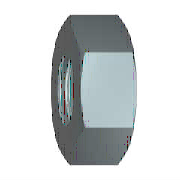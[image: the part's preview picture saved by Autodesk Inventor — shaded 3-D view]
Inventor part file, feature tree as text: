
AUTODESK INVENTOR PART (.ipt)
format: ipt  version: 2024.3 (Build 283343000, 343)  size: 161,280 bytes
history: native  units: mm (DEFAULTED — no unit token found)
features: chamfer x1, hole x1, other x1, plane x1
ambient origin geometry x7: Origin, YZ Plane, XZ Plane, X Axis, Y Axis, Z Axis, Center Point
bodies: Solid1 (feature_tree), Body (feature_tree)
feature tree (4):
  chamfer  "Chamfer1"  Distance=6.350853mm
  hole  "Thread"  [1 undecoded]
  other  "Work Axis1"
  plane  "Work Plane1"
note: 1 required parameter value undecoded (feature->parameter linkage not recoverable at this tier; creation-order binding heuristic only, values carry confidence <= 0.55)
